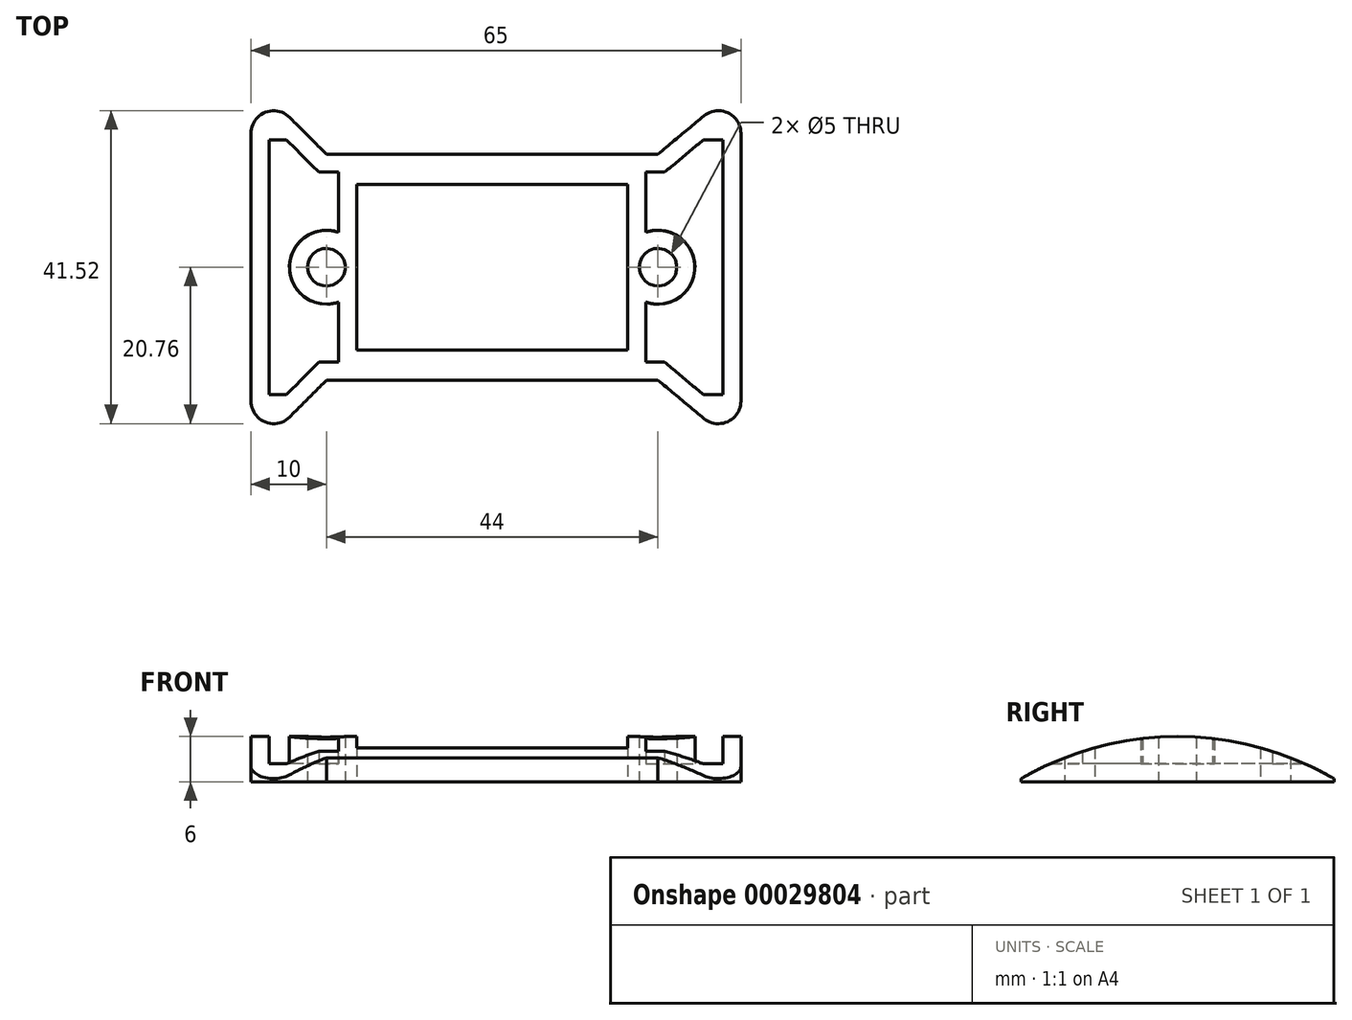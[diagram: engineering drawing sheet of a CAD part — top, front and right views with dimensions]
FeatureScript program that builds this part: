
annotation { "Feature Type Name" : "Feature", "Feature Type Description" : "" }
export const myFeature = defineFeature(function(context is Context, id is Id, definition is map)
    precondition{}
    {
        {
            var Q0;
            Q0=qCreatedBy(makeId("Top.planeOp"),FACE);
            var sketch = newSketch(context, id + "F0", { "sketchPlane" : qUnion([Q0])});
            skLineSegment(sketch, "E0.bottom", {"start": v(-54, 40) * mm, "end": v(0, 40) * mm, "construction": true});
            skLineSegment(sketch, "E0.top", {"start": v(-54, 0) * mm, "end": v(0, 0) * mm, "construction": true});
            skLineSegment(sketch, "E0.left", {"start": v(-54, 40) * mm, "end": v(-54, 0) * mm, "construction": true});
            skLineSegment(sketch, "E0.right", {"start": v(0, 40) * mm, "end": v(0, 0) * mm, "construction": true});
            skLineSegment(sketch, "E1.1", {"start": v(-59, 37.76) * mm, "end": v(-59, 2.24) * mm});
            skLineSegment(sketch, "E1.3", {"start": v(6, 37.76) * mm, "end": v(6, 2.24) * mm});
            skLineSegment(sketch, "E2.0", {"start": v(-49, 35) * mm, "end": v(-5, 35) * mm});
            skLineSegment(sketch, "E2.1", {"start": v(-49, 35) * mm, "end": v(-49, 5) * mm});
            skLineSegment(sketch, "E2.2", {"start": v(-49, 5) * mm, "end": v(-5, 5) * mm});
            skLineSegment(sketch, "E2.3", {"start": v(-5, 35) * mm, "end": v(-5, 5) * mm});
            skLineSegment(sketch, "E3", {"start": v(-53.88, 39.88) * mm, "end": v(-49, 35) * mm});
            skLineSegment(sketch, "E4", {"start": v(-49, 5) * mm, "end": v(-53.88, 0.12) * mm});
            skLineSegment(sketch, "E5", {"start": v(1.08, -0.06) * mm, "end": v(-5, 5) * mm});
            skLineSegment(sketch, "E6", {"start": v(-5, 35) * mm, "end": v(1.08, 40.06) * mm});
            skPoint(sketch, "E7.visualSharp", {"position": v(-59, 45) * mm});
            skArc(sketch, "E7.filletArc", {"start": v(-53.88, 39.88) * mm, "mid": v(-57.15, 40.53) * mm, "end": v(-59, 37.76) * mm});
            skPoint(sketch, "E8.visualSharp", {"position": v(-59, -5) * mm});
            skArc(sketch, "E8.filletArc", {"start": v(-59, 2.24) * mm, "mid": v(-57.15, -0.53) * mm, "end": v(-53.88, 0.12) * mm});
            skPoint(sketch, "E9.visualSharp", {"position": v(6, 44.16) * mm});
            skArc(sketch, "E9.filletArc", {"start": v(6, 37.76) * mm, "mid": v(4.27, 40.47) * mm, "end": v(1.08, 40.06) * mm});
            skPoint(sketch, "E10.visualSharp", {"position": v(6, -4.16) * mm});
            skArc(sketch, "E10.filletArc", {"start": v(1.08, -0.06) * mm, "mid": v(4.27, -0.47) * mm, "end": v(6, 2.24) * mm});
            skCircle(sketch, "E11", {"center": v(-49, 20) * mm, "radius": 2.5 * mm});
            skCircle(sketch, "E12", {"center": v(-5, 20) * mm, "radius": 2.5 * mm});
            skLineSegment(sketch, "E13.0", {"start": v(-45, 31) * mm, "end": v(-45, 9) * mm});
            skLineSegment(sketch, "E13.1", {"start": v(-45, 31) * mm, "end": v(-9, 31) * mm});
            skLineSegment(sketch, "E13.2", {"start": v(-9, 31) * mm, "end": v(-9, 9) * mm});
            skLineSegment(sketch, "E13.3", {"start": v(-45, 9) * mm, "end": v(-9, 9) * mm});
            skSolve(sketch);
        }
        {
            var Q0;
            Q0=makeQuery(id+"F0.imprint","IMPRINT",FACE,{"disambiguationData":[TD([[makeQuery(id+"F0.imprint","IMPRINT",EDGE,{"derivedFrom":sQuery(id+"F0.wireOp",EDGE,"E1.1")}),1.0]])]});
            var Q1;
            Q1=makeQuery(id+"F0.imprint","IMPRINT",FACE,{"disambiguationData":[TD([[makeQuery(id+"F0.imprint","IMPRINT",EDGE,{"derivedFrom":sQuery(id+"F0.wireOp",EDGE,"E2.0")}),-1.0]])]});
            var Q2;
            Q2=makeQuery(id+"F0.imprint","IMPRINT",FACE,{"disambiguationData":[TD([[makeQuery(id+"F0.imprint","IMPRINT",EDGE,{"derivedFrom":sQuery(id+"F0.wireOp",EDGE,"E1.3")}),-1.0]])]});
            extrude(context, id + "F1", {"entities" : qUnion([Q0, Q1, Q2]), "depth" : 2 * mm});
        }
        {
            var Q0;
            Q0=makeQuery(id+"F1.opExtrude","SWEPT_FACE",FACE,{"disambiguationData":[OSD([sQuery(id+"F0.wireOp",EDGE,"E1.1")])]});
            var sketch = newSketch(context, id + "F2", { "sketchPlane" : qUnion([Q0])});
            skArc(sketch, "E14", {"start": v(-2.24, 2) * mm, "mid": v(-20, 6) * mm, "end": v(-37.76, 2) * mm});
            skSolve(sketch);
        }
        {
            var Q0;
            Q0 = qSketchRegion(id + "F2", true);
            var Q1;
            Q1=makeQuery(id+"F2.imprint","IMPRINT",FACE,{"disambiguationData":[TD([[makeQuery(id+"F2.imprint","IMPRINT",EDGE,{"derivedFrom":sQuery(id+"F2.wireOp",EDGE,"E14")}),1.0]])]});
            extrude(context, id + "F3", {"entities" : qUnion([Q0, Q1]), "oppositeDirection" : true, "depth" : 65 * mm});
        }
        {
            var Q0;
            Q0 = qSketchRegion(id + "F0", true);
            extrude(context, id + "F4", {"entities" : qUnion([Q0]), "operationType" : NewBodyOperationType.INTERSECT, "depth" : 25 * mm});
        }
        {
            var Q0;
            Q0=makeQuery(id+"F3.opExtrude","SWEPT_BODY",BODY,{"disambiguationData":[OSD([sQuery(id+"F0.wireOp",EDGE,"E1.1"),sQuery(id+"F2.wireOp",EDGE,"E14")])]});
            var Q1;
            Q1=makeQuery(id+"F1.opExtrude","SWEPT_BODY",BODY,{"disambiguationData":[OSD([sQuery(id+"F0.wireOp",EDGE,"E1.1"),sQuery(id+"F0.wireOp",EDGE,"E1.3"),sQuery(id+"F0.wireOp",EDGE,"E2.0"),sQuery(id+"F0.wireOp",EDGE,"E2.2"),sQuery(id+"F0.wireOp",EDGE,"E3"),sQuery(id+"F0.wireOp",EDGE,"E4"),sQuery(id+"F0.wireOp",EDGE,"E5"),sQuery(id+"F0.wireOp",EDGE,"E6"),sQuery(id+"F0.wireOp",EDGE,"E7.filletArc"),sQuery(id+"F0.wireOp",EDGE,"E8.filletArc"),sQuery(id+"F0.wireOp",EDGE,"E9.filletArc"),sQuery(id+"F0.wireOp",EDGE,"E10.filletArc"),sQuery(id+"F0.wireOp",EDGE,"E11"),sQuery(id+"F0.wireOp",EDGE,"E12"),sQuery(id+"F0.wireOp",EDGE,"E13.0"),sQuery(id+"F0.wireOp",EDGE,"E13.1"),sQuery(id+"F0.wireOp",EDGE,"E13.2"),sQuery(id+"F0.wireOp",EDGE,"E13.3")])]});
            booleanBodies(context, id + "F5", {"operationType" : BooleanOperationType.UNION, "tools" : qUnion([Q0, Q1])});
        }
        {
            var Q0;
            {var subQ0=sQuery(id+"F0.wireOp",EDGE,"E1.1");Q0=makeQuery(id+"F5.opBoolean","MERGE",FACE,{"derivedFrom":[makeQuery(id+"F1.opExtrude","SWEPT_FACE",FACE,{"disambiguationData":[OSD([subQ0])]}),makeQuery(id+"F3.opExtrude","CAP_FACE",FACE,{"disambiguationData":[OSD([subQ0,sQuery(id+"F2.wireOp",EDGE,"E14")])],"isStart":true})]});}
            var sketch = newSketch(context, id + "F6", { "sketchPlane" : qUnion([Q0])});
            skArc(sketch, "E15.0", {"start": v(1.47, 0) * mm, "mid": v(-20, 6) * mm, "end": v(-41.47, 0) * mm});
            skLineSegment(sketch, "E16", {"start": v(-41.47, 0) * mm, "end": v(-41.47, 7.01) * mm});
            skLineSegment(sketch, "E17", {"start": v(-41.47, 7.01) * mm, "end": v(1.47, 7.01) * mm});
            skLineSegment(sketch, "E18", {"start": v(1.47, 7.01) * mm, "end": v(1.47, 0) * mm});
            skSolve(sketch);
        }
        {
            var Q0;
            Q0 = qSketchRegion(id + "F6", true);
            extrude(context, id + "F7", {"entities" : qUnion([Q0]), "operationType" : NewBodyOperationType.REMOVE, "endBound" : BoundingType.THROUGH_ALL, "oppositeDirection" : true, "depth" : 25 * mm});
        }
        {
            var Q0;
            Q0=makeQuery(id+"F7.boolean.opBoolean","MERGE",FACE,{"derivedFrom":[makeQuery(id+"F3.opExtrude","SWEPT_FACE",FACE,{"disambiguationData":[OSD([sQuery(id+"F2.wireOp",EDGE,"E14")])]}),makeQuery(id+"F7.opExtrude","SWEPT_FACE",FACE,{"disambiguationData":[OSD([sQuery(id+"F6.wireOp",EDGE,"E15.0")])]})]});
            shell(context, id + "F8", {"entities" : qUnion([Q0]), "thickness" : 2.4 * mm});
        }
    });
